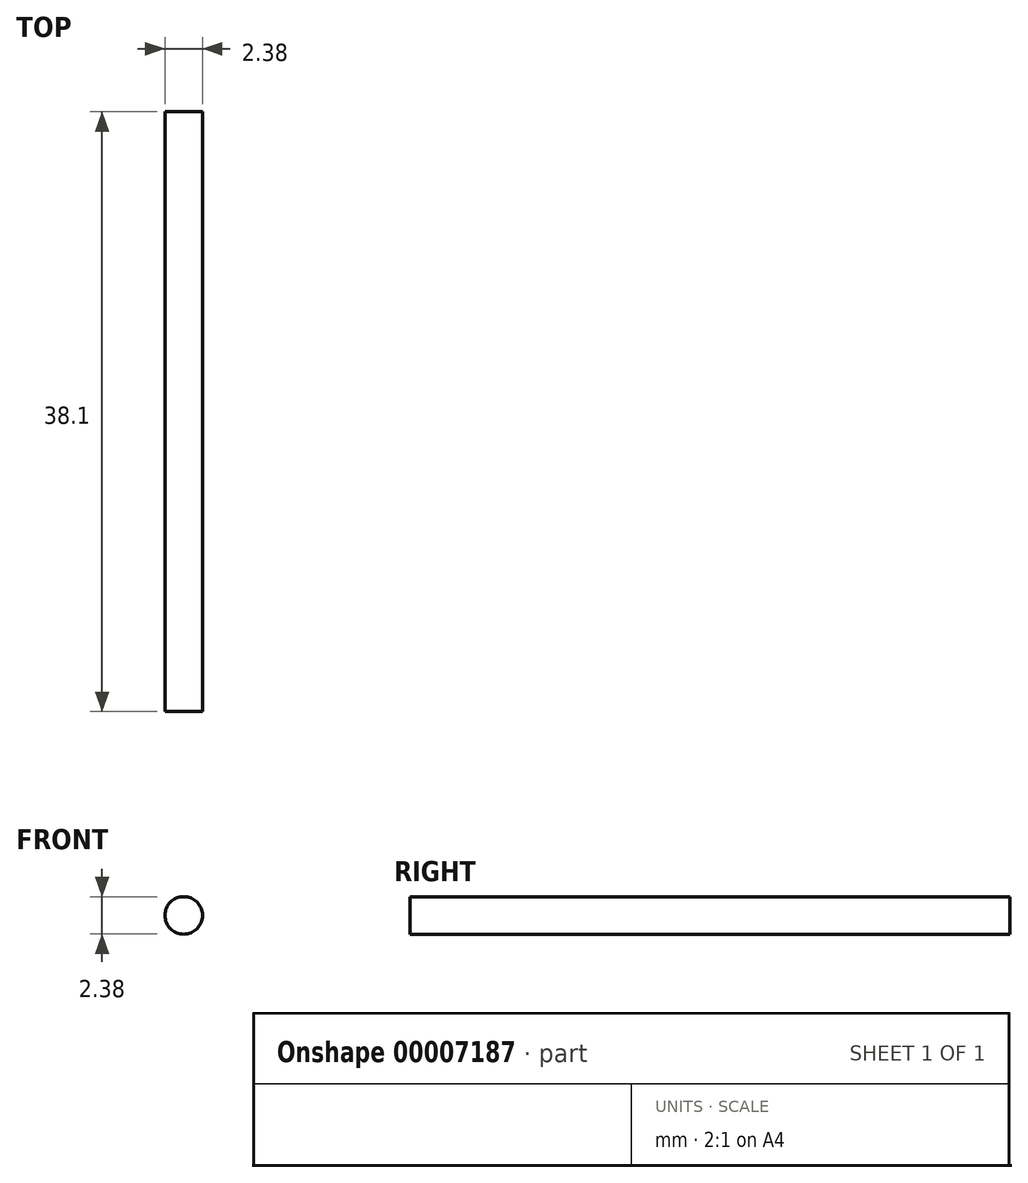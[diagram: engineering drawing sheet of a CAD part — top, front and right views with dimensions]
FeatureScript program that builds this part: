
annotation { "Feature Type Name" : "Feature", "Feature Type Description" : "" }
export const myFeature = defineFeature(function(context is Context, id is Id, definition is map)
    precondition{}
    {
        {
            var Q0;
            Q0=qCreatedBy(makeId("Front.planeOp"),FACE);
            var sketch = newSketch(context, id + "F0", { "sketchPlane" : qUnion([Q0])});
            skCircle(sketch, "E0", {"center": v(0, 0) * mm, "radius": 1.2 * mm});
            skSolve(sketch);
        }
        {
            var Q0;
            Q0 = qSketchRegion(id + "F0", true);
            extrude(context, id + "F1", {"entities" : qUnion([Q0]), "depth" : 38.1 * mm});
        }
    });
